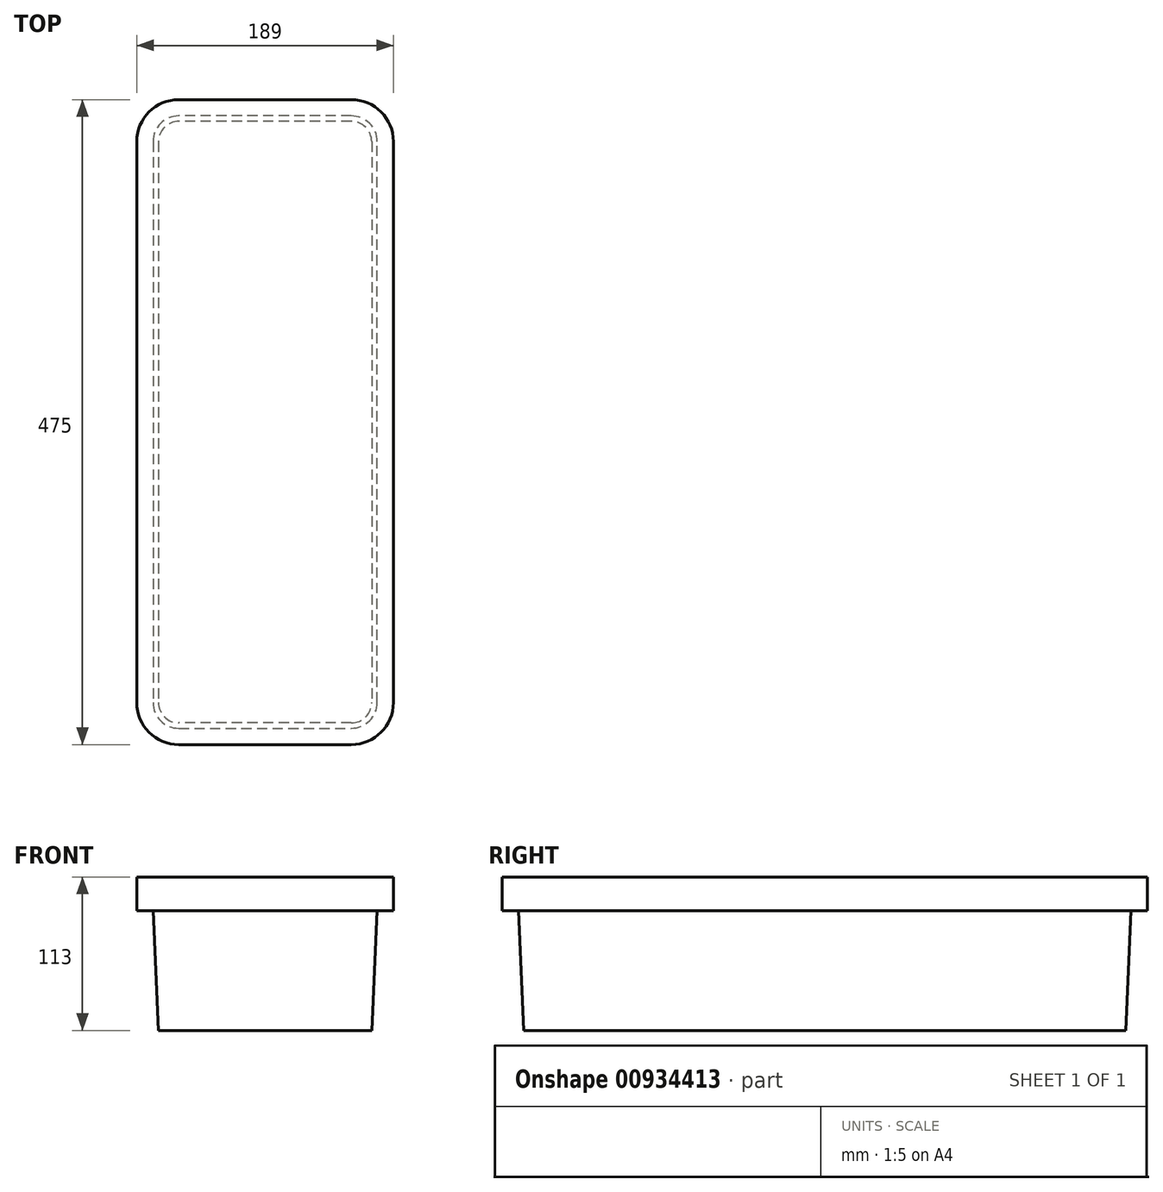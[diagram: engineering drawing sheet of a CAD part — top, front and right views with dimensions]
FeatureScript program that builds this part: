
annotation { "Feature Type Name" : "Feature", "Feature Type Description" : "" }
export const myFeature = defineFeature(function(context is Context, id is Id, definition is map)
    precondition{}
    {
        {
            var Q0;
            Q0=qCreatedBy(makeId("Top.planeOp"),FACE);
            var sketch = newSketch(context, id + "F0", { "sketchPlane" : qUnion([Q0])});
            skLineSegment(sketch, "E0.bottom", {"start": v(63.5, 221.5) * mm, "end": v(-63.5, 221.5) * mm});
            skLineSegment(sketch, "E0.top", {"start": v(63.5, -221.5) * mm, "end": v(-63.5, -221.5) * mm});
            skLineSegment(sketch, "E0.left", {"start": v(78.5, 206.5) * mm, "end": v(78.5, -206.5) * mm});
            skLineSegment(sketch, "E0.right", {"start": v(-78.5, 206.5) * mm, "end": v(-78.5, -206.5) * mm});
            skPoint(sketch, "E0.middle", {"position": v(0, 0) * mm});
            skPoint(sketch, "E1.visualSharp", {"position": v(-78.5, 221.5) * mm});
            skArc(sketch, "E1.filletArc", {"start": v(-63.5, 221.5) * mm, "mid": v(-74.1, 217.1) * mm, "end": v(-78.5, 206.5) * mm});
            skPoint(sketch, "E2.visualSharp", {"position": v(78.5, 221.5) * mm});
            skArc(sketch, "E2.filletArc", {"start": v(78.5, 206.5) * mm, "mid": v(74.1, 217.1) * mm, "end": v(63.5, 221.5) * mm});
            skPoint(sketch, "E3.visualSharp", {"position": v(78.5, -221.5) * mm});
            skArc(sketch, "E3.filletArc", {"start": v(63.5, -221.5) * mm, "mid": v(74.1, -217.1) * mm, "end": v(78.5, -206.5) * mm});
            skPoint(sketch, "E4.visualSharp", {"position": v(-78.5, -221.5) * mm});
            skArc(sketch, "E4.filletArc", {"start": v(-78.5, -206.5) * mm, "mid": v(-74.1, -217.1) * mm, "end": v(-63.5, -221.5) * mm});
            skSolve(sketch);
        }
        {
            var Q0;
            Q0=makeQuery(id+"F0.imprint","IMPRINT",FACE,{"disambiguationData":[TD([[makeQuery(id+"F0.imprint","IMPRINT",EDGE,{"derivedFrom":sQuery(id+"F0.wireOp",EDGE,"E0.bottom")}),1.0]])]});
            cPlane(context, id + "F1", {"entities" : qUnion([Q0]), "cplaneType" : CPlaneType.OFFSET, "offset" : 88 * mm, "width" : 150 * mm, "height" : 150 * mm});
        }
        {
            var Q0;
            Q0=qCreatedBy(id+"F1.planeOp",FACE);
            var sketch = newSketch(context, id + "F2", { "sketchPlane" : qUnion([Q0])});
            skArc(sketch, "E5.0", {"start": v(-82.5, -206.5) * mm, "mid": v(-76.94, -219.94) * mm, "end": v(-63.5, -225.5) * mm});
            skLineSegment(sketch, "E5.1", {"start": v(-82.5, 206.5) * mm, "end": v(-82.5, -206.5) * mm});
            skLineSegment(sketch, "E5.2", {"start": v(-63.5, -225.5) * mm, "end": v(63.5, -225.5) * mm});
            skArc(sketch, "E5.3", {"start": v(-63.5, 225.5) * mm, "mid": v(-76.94, 219.94) * mm, "end": v(-82.5, 206.5) * mm});
            skArc(sketch, "E5.4", {"start": v(63.5, -225.5) * mm, "mid": v(76.94, -219.94) * mm, "end": v(82.5, -206.5) * mm});
            skLineSegment(sketch, "E5.5", {"start": v(82.5, -206.5) * mm, "end": v(82.5, 206.5) * mm});
            skArc(sketch, "E5.6", {"start": v(82.5, 206.5) * mm, "mid": v(76.94, 219.94) * mm, "end": v(63.5, 225.5) * mm});
            skLineSegment(sketch, "E5.7", {"start": v(63.5, 225.5) * mm, "end": v(-63.5, 225.5) * mm});
            skSolve(sketch);
        }
        {
            var Q0;
            Q0=makeQuery(id+"F2.imprint","IMPRINT",FACE,{"disambiguationData":[TD([[makeQuery(id+"F2.imprint","IMPRINT",EDGE,{"derivedFrom":sQuery(id+"F2.wireOp",EDGE,"E5.0")}),1.0]])]});
            var Q1;
            Q1=makeQuery(id+"F0.imprint","IMPRINT",FACE,{"disambiguationData":[TD([[makeQuery(id+"F0.imprint","IMPRINT",EDGE,{"derivedFrom":sQuery(id+"F0.wireOp",EDGE,"E0.bottom")}),1.0]])]});
            loft(context, id + "F3", {"sheetProfilesArray" : [{ "sheetProfileEntities" : qUnion([Q0]) }, { "sheetProfileEntities" : qUnion([Q1]) }]});
        }
        {
            var Q0;
            Q0=makeQuery(id+"F3.opLoft","CAP_FACE",FACE,{"disambiguationData":[OSD([makeQuery(id+"F2.imprint","IMPRINT",FACE,{"disambiguationData":[TD([[makeQuery(id+"F2.imprint","IMPRINT",EDGE,{"derivedFrom":sQuery(id+"F2.wireOp",EDGE,"E5.0")}),1.0]])]})])],"isStart":true});
            var sketch = newSketch(context, id + "F4", { "sketchPlane" : qUnion([Q0])});
            skLineSegment(sketch, "E6.0", {"start": v(-63.5, 237.5) * mm, "end": v(63.5, 237.5) * mm});
            skArc(sketch, "E6.1", {"start": v(-94.5, 206.5) * mm, "mid": v(-85.42, 228.42) * mm, "end": v(-63.5, 237.5) * mm});
            skArc(sketch, "E6.2", {"start": v(63.5, 237.5) * mm, "mid": v(85.42, 228.42) * mm, "end": v(94.5, 206.5) * mm});
            skLineSegment(sketch, "E6.3", {"start": v(-94.5, -206.5) * mm, "end": v(-94.5, 206.5) * mm});
            skLineSegment(sketch, "E6.4", {"start": v(94.5, 206.5) * mm, "end": v(94.5, -206.5) * mm});
            skArc(sketch, "E6.5", {"start": v(94.5, -206.5) * mm, "mid": v(85.42, -228.42) * mm, "end": v(63.5, -237.5) * mm});
            skLineSegment(sketch, "E6.6", {"start": v(63.5, -237.5) * mm, "end": v(-63.5, -237.5) * mm});
            skArc(sketch, "E6.7", {"start": v(-63.5, -237.5) * mm, "mid": v(-85.42, -228.42) * mm, "end": v(-94.5, -206.5) * mm});
            skSolve(sketch);
        }
        {
            var Q0;
            Q0 = qSketchRegion(id + "F4", true);
            extrude(context, id + "F5", {"entities" : qUnion([Q0]), "operationType" : NewBodyOperationType.ADD, "depth" : 25 * mm, "offsetDistance" : 25 * mm});
        }
    });
